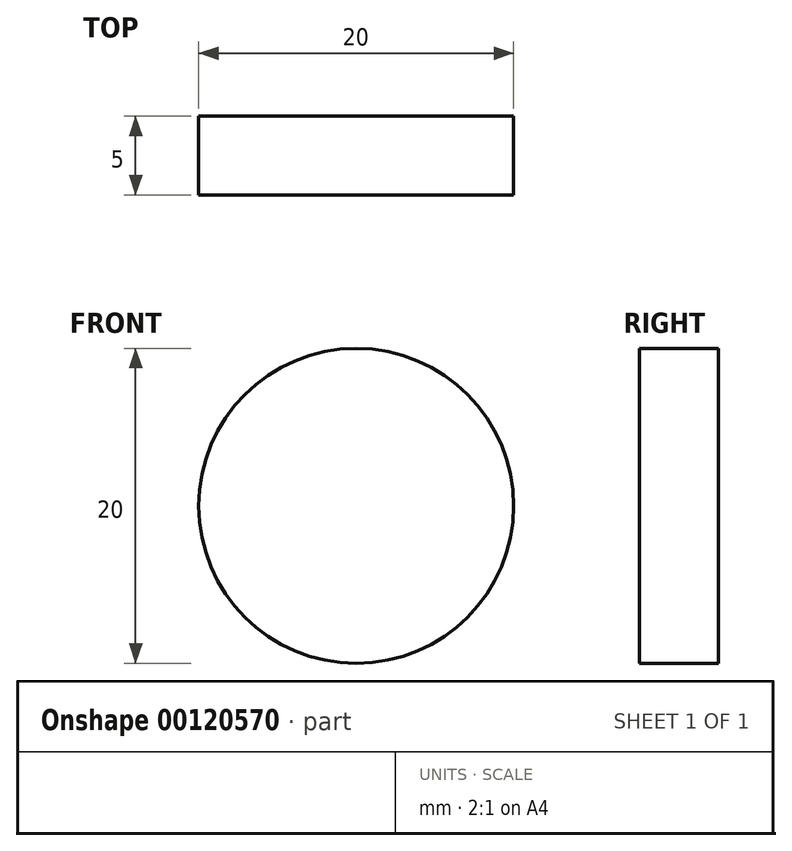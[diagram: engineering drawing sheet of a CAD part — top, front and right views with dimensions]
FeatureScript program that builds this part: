
annotation { "Feature Type Name" : "Feature", "Feature Type Description" : "" }
export const myFeature = defineFeature(function(context is Context, id is Id, definition is map)
    precondition{}
    {
        {
            var Q0;
            Q0=qCreatedBy(makeId("Front.planeOp"),FACE);
            var sketch = newSketch(context, id + "F0", { "sketchPlane" : qUnion([Q0])});
            skCircle(sketch, "E0", {"center": v(0, 0) * mm, "radius": 10 * mm});
            skSolve(sketch);
        }
        {
            var Q0;
            Q0=makeQuery(id+"F0.imprint","IMPRINT",FACE,{"disambiguationData":[TD([[makeQuery(id+"F0.imprint","IMPRINT",EDGE,{"derivedFrom":sQuery(id+"F0.wireOp",EDGE,"E0")}),1.0]])]});
            extrude(context, id + "F1", {"entities" : qUnion([Q0]), "depth" : 5 * mm});
        }
    });
